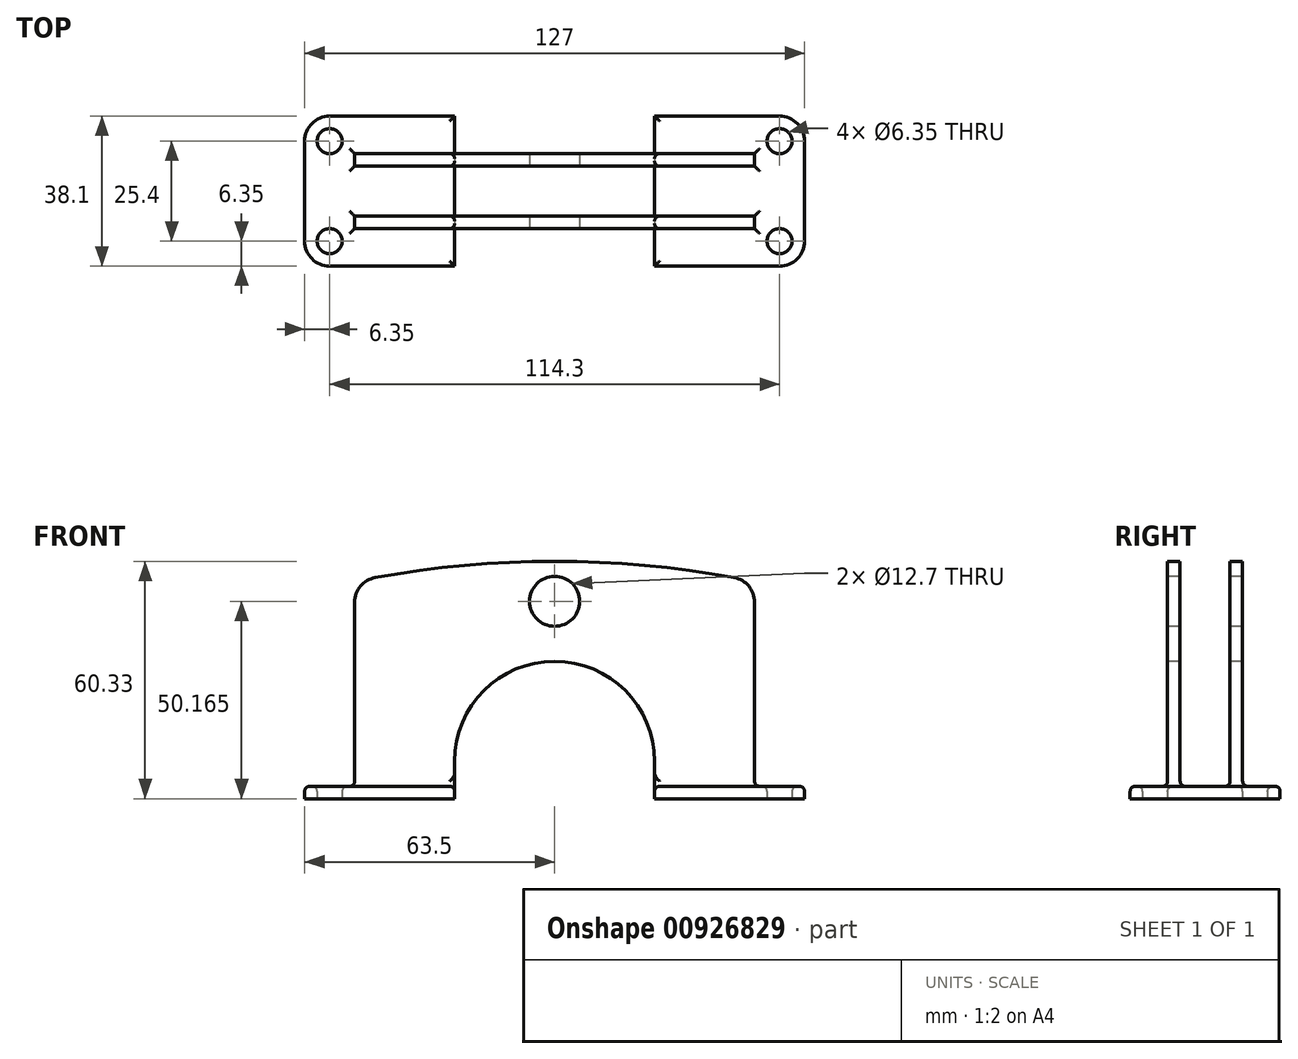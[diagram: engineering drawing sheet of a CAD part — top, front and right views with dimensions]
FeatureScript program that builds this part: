
annotation { "Feature Type Name" : "Feature", "Feature Type Description" : "" }
export const myFeature = defineFeature(function(context is Context, id is Id, definition is map)
    precondition{}
    {
        {
            var Q0;
            Q0=qCreatedBy(makeId("Top.planeOp"),FACE);
            var sketch = newSketch(context, id + "F0", { "sketchPlane" : qUnion([Q0])});
            skLineSegment(sketch, "E0.bottom", {"start": v(-57.15, 19.05) * mm, "end": v(57.15, 19.05) * mm});
            skLineSegment(sketch, "E0.top", {"start": v(-57.15, -19.05) * mm, "end": v(57.15, -19.05) * mm});
            skLineSegment(sketch, "E0.left", {"start": v(-63.5, 12.7) * mm, "end": v(-63.5, -12.7) * mm});
            skLineSegment(sketch, "E0.right", {"start": v(63.5, 12.7) * mm, "end": v(63.5, -12.7) * mm});
            skCircle(sketch, "E1", {"center": v(-57.15, -12.7) * mm, "radius": 3.18 * mm});
            skCircle(sketch, "E2", {"center": v(-57.15, 12.7) * mm, "radius": 3.18 * mm});
            skCircle(sketch, "E3", {"center": v(57.15, 12.7) * mm, "radius": 3.18 * mm});
            skCircle(sketch, "E4", {"center": v(57.15, -12.7) * mm, "radius": 3.18 * mm});
            skPoint(sketch, "E5.visualSharp", {"position": v(-63.5, 19.05) * mm});
            skArc(sketch, "E5.filletArc", {"start": v(-57.15, 19.05) * mm, "mid": v(-61.64, 17.2) * mm, "end": v(-63.5, 12.7) * mm});
            skPoint(sketch, "E6.visualSharp", {"position": v(-63.5, -19.05) * mm});
            skArc(sketch, "E6.filletArc", {"start": v(-63.5, -12.7) * mm, "mid": v(-61.64, -17.2) * mm, "end": v(-57.15, -19.05) * mm});
            skPoint(sketch, "E7.visualSharp", {"position": v(63.5, -19.05) * mm});
            skArc(sketch, "E7.filletArc", {"start": v(57.15, -19.05) * mm, "mid": v(61.64, -17.2) * mm, "end": v(63.5, -12.7) * mm});
            skPoint(sketch, "E8.visualSharp", {"position": v(63.5, 19.05) * mm});
            skArc(sketch, "E8.filletArc", {"start": v(63.5, 12.7) * mm, "mid": v(61.64, 17.2) * mm, "end": v(57.15, 19.05) * mm});
            skSolve(sketch);
        }
        {
            var Q0;
            Q0=makeQuery(id+"F0.imprint","IMPRINT",FACE,{"disambiguationData":[TD([[makeQuery(id+"F0.imprint","IMPRINT",EDGE,{"derivedFrom":sQuery(id+"F0.wireOp",EDGE,"E0.bottom")}),-1.0]])]});
            extrude(context, id + "F1", {"entities" : qUnion([Q0]), "depth" : 3.17 * mm, "offsetDistance" : 25.4 * mm});
        }
        {
            var Q0;
            Q0=makeQuery(id+"F1.opExtrude","CAP_FACE",FACE,{"disambiguationData":[OSD([sQuery(id+"F0.wireOp",EDGE,"E0.bottom"),sQuery(id+"F0.wireOp",EDGE,"E0.top"),sQuery(id+"F0.wireOp",EDGE,"E0.left"),sQuery(id+"F0.wireOp",EDGE,"E0.right"),sQuery(id+"F0.wireOp",EDGE,"E1"),sQuery(id+"F0.wireOp",EDGE,"E2"),sQuery(id+"F0.wireOp",EDGE,"E3"),sQuery(id+"F0.wireOp",EDGE,"E4"),sQuery(id+"F0.wireOp",EDGE,"E5.filletArc"),sQuery(id+"F0.wireOp",EDGE,"E6.filletArc"),sQuery(id+"F0.wireOp",EDGE,"E7.filletArc"),sQuery(id+"F0.wireOp",EDGE,"E8.filletArc")])],"isStart":false});
            var sketch = newSketch(context, id + "F2", { "sketchPlane" : qUnion([Q0])});
            skLineSegment(sketch, "E9", {"start": v(-25.4, 19.05) * mm, "end": v(-25.4, -19.05) * mm});
            skLineSegment(sketch, "E10", {"start": v(25.4, 19.05) * mm, "end": v(25.4, -19.05) * mm});
            skSolve(sketch);
        }
        {
            var Q0;
            {var subQ0=sQuery(id+"F2.wireOp",EDGE,"E9");Q0=makeQuery(id+"F2.imprint","IMPRINT",FACE,{"disambiguationData":[TD([[makeQuery(id+"F2.imprint","IMPRINT",EDGE,{"derivedFrom":subQ0}),1.0]])]});}
            extrude(context, id + "F3", {"entities" : qUnion([Q0]), "operationType" : NewBodyOperationType.REMOVE, "endBound" : BoundingType.THROUGH_ALL, "oppositeDirection" : true, "depth" : 25.4 * mm, "offsetDistance" : 25.4 * mm});
        }
        {
            var Q0;
            {var subQ2=sQuery(id+"F0.wireOp",EDGE,"E6.filletArc");var subQ10=sQuery(id+"F0.wireOp",EDGE,"E0.top");Q0=makeQuery(id+"F3.boolean.opBoolean","SPLIT",FACE,{"disambiguationData":[TD([makeQuery(id+"F1.opExtrude","SWEPT_FACE",FACE,{"disambiguationData":[OSD([subQ2])]})])],"derivedFrom":makeQuery(id+"F1.opExtrude","SWEPT_FACE",FACE,{"disambiguationData":[OSD([subQ10])]})});}
            var sketch = newSketch(context, id + "F4", { "sketchPlane" : qUnion([Q0])});
            skLineSegment(sketch, "E11", {"start": v(-50.8, 3.18) * mm, "end": v(-50.8, 49.95) * mm});
            skLineSegment(sketch, "E12", {"start": v(-50.8, 60.33) * mm, "end": v(50.8, 60.33) * mm});
            skLineSegment(sketch, "E13", {"start": v(50.8, 49.95) * mm, "end": v(50.8, 3.18) * mm});
            skArc(sketch, "E14", {"start": v(-45.59, 56.2) * mm, "mid": v(0, 60.33) * mm, "end": v(45.59, 56.2) * mm});
            skPoint(sketch, "E15.newPointA", {"position": v(-50.8, 60.33) * mm});
            skArc(sketch, "E15.filletArc", {"start": v(-45.59, 56.2) * mm, "mid": v(-49.33, 54.02) * mm, "end": v(-50.8, 49.95) * mm});
            skArc(sketch, "E16.filletArc", {"start": v(50.8, 49.95) * mm, "mid": v(49.33, 54.02) * mm, "end": v(45.59, 56.2) * mm});
            skCircle(sketch, "E17", {"center": v(0, 50.16) * mm, "radius": 6.35 * mm});
            skCircle(sketch, "E18", {"center": v(0, 50.16) * mm, "radius": 41.28 * mm});
            skLineSegment(sketch, "E19", {"start": v(-51.77, 91.44) * mm, "end": v(53.8, 91.44) * mm});
            skLineSegment(sketch, "E20", {"start": v(-25.4, 3.18) * mm, "end": v(-25.4, 9.53) * mm});
            skCircle(sketch, "E21", {"center": v(0, 9.53) * mm, "radius": 25.4 * mm});
            skLineSegment(sketch, "E22", {"start": v(25.4, 9.53) * mm, "end": v(25.4, 3.17) * mm});
            skLineSegment(sketch, "E23", {"start": v(50.8, 3.18) * mm, "end": v(25.4, 3.17) * mm});
            skPoint(sketch, "E24.orphan", {"position": v(25.4, 0) * mm});
            skSolve(sketch);
        }
        {
            var Q0;
            Q0=makeQuery(id+"F4.imprint","IMPRINT",FACE,{"disambiguationData":[TD([[makeQuery(id+"F4.imprint","IMPRINT",EDGE,{"derivedFrom":sQuery(id+"F4.wireOp",EDGE,"E13")}),-1.0]])]});
            var Q1;
            Q1=makeQuery(id+"F4.imprint","IMPRINT",FACE,{"disambiguationData":[TD([[makeQuery(id+"F4.imprint","IMPRINT",EDGE,{"derivedFrom":sQuery(id+"F4.wireOp",EDGE,"E17")}),-1.0]])]});
            var Q2;
            {var subQ6=sQuery(id+"F4.wireOp",EDGE,"E11");Q2=makeQuery(id+"F4.imprint","IMPRINT",FACE,{"disambiguationData":[TD([[makeQuery(id+"F4.imprint","IMPRINT",EDGE,{"derivedFrom":subQ6}),-1.0]])]});}
            var Q3;
            {var subQ3=sQuery(id+"F0.wireOp",EDGE,"E5.filletArc");var subQ11=sQuery(id+"F0.wireOp",EDGE,"E0.bottom");Q3=makeQuery(id+"F3.boolean.opBoolean","SPLIT",FACE,{"disambiguationData":[TD([makeQuery(id+"F1.opExtrude","SWEPT_FACE",FACE,{"disambiguationData":[OSD([subQ3])]})])],"derivedFrom":makeQuery(id+"F1.opExtrude","SWEPT_FACE",FACE,{"disambiguationData":[OSD([subQ11])]})});}
            extrude(context, id + "F5", {"entities" : qUnion([Q0, Q1, Q2]), "operationType" : NewBodyOperationType.ADD, "endBound" : BoundingType.UP_TO_SURFACE, "oppositeDirection" : true, "depth" : 25.4 * mm, "endBoundEntityFace" : qUnion([Q3]), "offsetDistance" : 25.4 * mm});
        }
        {
            var Q0;
            Q0=makeQuery(id+"F5.opExtrude","SWEPT_FACE",FACE,{"disambiguationData":[OSD([sQuery(id+"F4.wireOp",EDGE,"E13")])]});
            var sketch = newSketch(context, id + "F6", { "sketchPlane" : qUnion([Q0])});
            skLineSegment(sketch, "E25.bottom", {"start": v(-9.53, 3.17) * mm, "end": v(-6.35, 3.17) * mm});
            skLineSegment(sketch, "E25.top", {"start": v(-9.53, 104.78) * mm, "end": v(-6.35, 104.78) * mm});
            skLineSegment(sketch, "E25.left", {"start": v(-9.53, 3.17) * mm, "end": v(-9.53, 104.78) * mm});
            skLineSegment(sketch, "E25.right", {"start": v(-6.35, 3.17) * mm, "end": v(-6.35, 104.78) * mm});
            skLineSegment(sketch, "E26.bottom", {"start": v(6.35, 3.17) * mm, "end": v(9.53, 3.17) * mm});
            skLineSegment(sketch, "E26.top", {"start": v(6.35, 104.78) * mm, "end": v(9.52, 104.78) * mm});
            skLineSegment(sketch, "E26.left", {"start": v(6.35, 3.17) * mm, "end": v(6.35, 104.78) * mm});
            skLineSegment(sketch, "E26.right", {"start": v(9.53, 3.17) * mm, "end": v(9.52, 104.78) * mm});
            skLineSegment(sketch, "E27.bottom", {"start": v(-19.05, 3.17) * mm, "end": v(19.05, 3.17) * mm});
            skLineSegment(sketch, "E27.top", {"start": v(-19.05, 104.78) * mm, "end": v(19.05, 104.78) * mm});
            skLineSegment(sketch, "E27.left", {"start": v(-19.05, 3.17) * mm, "end": v(-19.05, 104.78) * mm});
            skLineSegment(sketch, "E27.right", {"start": v(19.05, 3.17) * mm, "end": v(19.05, 104.78) * mm});
            skSolve(sketch);
        }
        {
            var Q0;
            {var subQ0=sQuery(id+"F6.wireOp",EDGE,"E27.bottom");var subQ5=sQuery(id+"F6.wireOp",EDGE,"E27.left");var subQ6=makeQuery(id+"F6.imprint","INTERSECT",VERTEX,{"derivedFrom":[subQ0,subQ5]});Q0=makeQuery(id+"F6.imprint","IMPRINT",FACE,{"disambiguationData":[TD([[makeQuery(id+"F6.imprint","IMPRINT",EDGE,{"disambiguationData":[TD([[subQ6,1.0]])],"derivedFrom":subQ0}),-1.0]])]});}
            var Q1;
            {var subQ0=sQuery(id+"F6.wireOp",EDGE,"E27.top");var subQ1=sQuery(id+"F6.wireOp",EDGE,"E25.left");var subQ2=makeQuery(id+"F6.imprint","INTERSECT",VERTEX,{"derivedFrom":[subQ1,subQ0]});Q1=makeQuery(id+"F6.imprint","IMPRINT",FACE,{"disambiguationData":[TD([[makeQuery(id+"F6.imprint","IMPRINT",EDGE,{"disambiguationData":[TD([[subQ2,1.0]])],"derivedFrom":subQ0}),-1.0]])]});}
            var Q2;
            {var subQ0=sQuery(id+"F6.wireOp",EDGE,"E27.bottom");var subQ5=sQuery(id+"F6.wireOp",EDGE,"E27.right");var subQ6=makeQuery(id+"F6.imprint","INTERSECT",VERTEX,{"derivedFrom":[subQ0,subQ5]});Q2=makeQuery(id+"F6.imprint","IMPRINT",FACE,{"disambiguationData":[TD([[makeQuery(id+"F6.imprint","IMPRINT",EDGE,{"disambiguationData":[TD([[subQ6,-1.0]])],"derivedFrom":subQ0}),-1.0]])]});}
            var Q3;
            {var subQ0=sQuery(id+"F6.wireOp",EDGE,"E27.top");var subQ1=sQuery(id+"F6.wireOp",EDGE,"E26.right");var subQ2=makeQuery(id+"F6.imprint","INTERSECT",VERTEX,{"derivedFrom":[subQ1,subQ0]});Q3=makeQuery(id+"F6.imprint","IMPRINT",FACE,{"disambiguationData":[TD([[makeQuery(id+"F6.imprint","IMPRINT",EDGE,{"disambiguationData":[TD([[subQ2,-1.0]])],"derivedFrom":subQ0}),-1.0]])]});}
            var Q4;
            {var subQ0=sQuery(id+"F6.wireOp",EDGE,"E27.bottom");var subQ1=sQuery(id+"F6.wireOp",EDGE,"E25.right");var subQ2=makeQuery(id+"F6.imprint","INTERSECT",VERTEX,{"derivedFrom":[subQ1,subQ0]});Q4=makeQuery(id+"F6.imprint","IMPRINT",FACE,{"disambiguationData":[TD([[makeQuery(id+"F6.imprint","IMPRINT",EDGE,{"disambiguationData":[TD([[subQ2,1.0]])],"derivedFrom":subQ0}),-1.0]])]});}
            var Q5;
            {var subQ0=sQuery(id+"F6.wireOp",EDGE,"E27.top");var subQ1=sQuery(id+"F6.wireOp",EDGE,"E25.right");var subQ2=makeQuery(id+"F6.imprint","INTERSECT",VERTEX,{"derivedFrom":[subQ1,subQ0]});Q5=makeQuery(id+"F6.imprint","IMPRINT",FACE,{"disambiguationData":[TD([[makeQuery(id+"F6.imprint","IMPRINT",EDGE,{"disambiguationData":[TD([[subQ2,-1.0]])],"derivedFrom":subQ0}),-1.0]])]});}
            extrude(context, id + "F7", {"entities" : qUnion([Q0, Q1, Q2, Q3, Q4, Q5]), "operationType" : NewBodyOperationType.REMOVE, "endBound" : BoundingType.THROUGH_ALL, "oppositeDirection" : true, "depth" : 25.4 * mm, "offsetDistance" : 25.4 * mm});
        }
        {
            var Q0;
            {var subQ0=sQuery(id+"F6.wireOp",EDGE,"E27.bottom");var subQ1=sQuery(id+"F0.wireOp",EDGE,"E1");var subQ2=sQuery(id+"F0.wireOp",EDGE,"E0.left");var subQ3=sQuery(id+"F0.wireOp",EDGE,"E0.top");var subQ4=sQuery(id+"F0.wireOp",EDGE,"E0.bottom");var subQ5=sQuery(id+"F0.wireOp",EDGE,"E6.filletArc");var subQ6=sQuery(id+"F0.wireOp",EDGE,"E2");var subQ7=sQuery(id+"F0.wireOp",EDGE,"E5.filletArc");Q0=makeQuery(id+"F7.boolean.opBoolean","MERGE",FACE,{"derivedFrom":[makeQuery(id+"F3.boolean.opBoolean","SPLIT",FACE,{"disambiguationData":[TD([makeQuery(id+"F1.opExtrude","SWEPT_FACE",FACE,{"disambiguationData":[OSD([subQ2])]})])],"derivedFrom":makeQuery(id+"F1.opExtrude","CAP_FACE",FACE,{"disambiguationData":[OSD([subQ4,subQ3,subQ2,sQuery(id+"F0.wireOp",EDGE,"E0.right"),subQ1,subQ6,sQuery(id+"F0.wireOp",EDGE,"E3"),sQuery(id+"F0.wireOp",EDGE,"E4"),subQ7,subQ5,sQuery(id+"F0.wireOp",EDGE,"E7.filletArc"),sQuery(id+"F0.wireOp",EDGE,"E8.filletArc")])],"isStart":false})})],"fromTools":[makeQuery(id+"F7.opExtrude","SWEPT_FACE",FACE,{"disambiguationData":[OSD([subQ0]),TDD([makeQuery(id+"F6.imprint","IMPRINT",EDGE,{"disambiguationData":[TD([[makeQuery(id+"F6.imprint","INTERSECT",VERTEX,{"derivedFrom":[subQ0,sQuery(id+"F6.wireOp",EDGE,"E27.right")]}),-1.0]])],"derivedFrom":subQ0})])]}),makeQuery(id+"F7.opExtrude","SWEPT_FACE",FACE,{"disambiguationData":[OSD([subQ0]),TDD([makeQuery(id+"F6.imprint","IMPRINT",EDGE,{"disambiguationData":[TD([[makeQuery(id+"F6.imprint","INTERSECT",VERTEX,{"derivedFrom":[sQuery(id+"F6.wireOp",EDGE,"E25.right"),subQ0]}),1.0]])],"derivedFrom":subQ0})])]}),makeQuery(id+"F7.opExtrude","SWEPT_FACE",FACE,{"disambiguationData":[OSD([subQ0]),TDD([makeQuery(id+"F6.imprint","IMPRINT",EDGE,{"disambiguationData":[TD([[makeQuery(id+"F6.imprint","INTERSECT",VERTEX,{"derivedFrom":[subQ0,sQuery(id+"F6.wireOp",EDGE,"E27.left")]}),1.0]])],"derivedFrom":subQ0})])]})]});}
            var Q1;
            {var subQ0=sQuery(id+"F6.wireOp",EDGE,"E27.bottom");var subQ1=sQuery(id+"F0.wireOp",EDGE,"E3");var subQ2=sQuery(id+"F0.wireOp",EDGE,"E0.top");var subQ3=sQuery(id+"F0.wireOp",EDGE,"E0.right");var subQ4=sQuery(id+"F0.wireOp",EDGE,"E0.bottom");var subQ5=sQuery(id+"F0.wireOp",EDGE,"E4");var subQ6=sQuery(id+"F0.wireOp",EDGE,"E7.filletArc");var subQ7=sQuery(id+"F0.wireOp",EDGE,"E8.filletArc");Q1=makeQuery(id+"F7.boolean.opBoolean","MERGE",FACE,{"derivedFrom":[makeQuery(id+"F3.boolean.opBoolean","SPLIT",FACE,{"disambiguationData":[TD([makeQuery(id+"F1.opExtrude","SWEPT_FACE",FACE,{"disambiguationData":[OSD([subQ3])]})])],"derivedFrom":makeQuery(id+"F1.opExtrude","CAP_FACE",FACE,{"disambiguationData":[OSD([subQ4,subQ2,sQuery(id+"F0.wireOp",EDGE,"E0.left"),subQ3,sQuery(id+"F0.wireOp",EDGE,"E1"),sQuery(id+"F0.wireOp",EDGE,"E2"),subQ1,subQ5,sQuery(id+"F0.wireOp",EDGE,"E5.filletArc"),sQuery(id+"F0.wireOp",EDGE,"E6.filletArc"),subQ6,subQ7])],"isStart":false})})],"fromTools":[makeQuery(id+"F7.opExtrude","SWEPT_FACE",FACE,{"disambiguationData":[OSD([subQ0]),TDD([makeQuery(id+"F6.imprint","IMPRINT",EDGE,{"disambiguationData":[TD([[makeQuery(id+"F6.imprint","INTERSECT",VERTEX,{"derivedFrom":[subQ0,sQuery(id+"F6.wireOp",EDGE,"E27.right")]}),-1.0]])],"derivedFrom":subQ0})])]}),makeQuery(id+"F7.opExtrude","SWEPT_FACE",FACE,{"disambiguationData":[OSD([subQ0]),TDD([makeQuery(id+"F6.imprint","IMPRINT",EDGE,{"disambiguationData":[TD([[makeQuery(id+"F6.imprint","INTERSECT",VERTEX,{"derivedFrom":[sQuery(id+"F6.wireOp",EDGE,"E25.right"),subQ0]}),1.0]])],"derivedFrom":subQ0})])]}),makeQuery(id+"F7.opExtrude","SWEPT_FACE",FACE,{"disambiguationData":[OSD([subQ0]),TDD([makeQuery(id+"F6.imprint","IMPRINT",EDGE,{"disambiguationData":[TD([[makeQuery(id+"F6.imprint","INTERSECT",VERTEX,{"derivedFrom":[subQ0,sQuery(id+"F6.wireOp",EDGE,"E27.left")]}),1.0]])],"derivedFrom":subQ0})])]})]});}
            fillet(context, id + "F8", {"entities" : qUnion([Q0, Q1]), "radius" : 1.27 * mm, "tangentPropagation" : true, "allowEdgeOverflow" : false});
        }
    });
